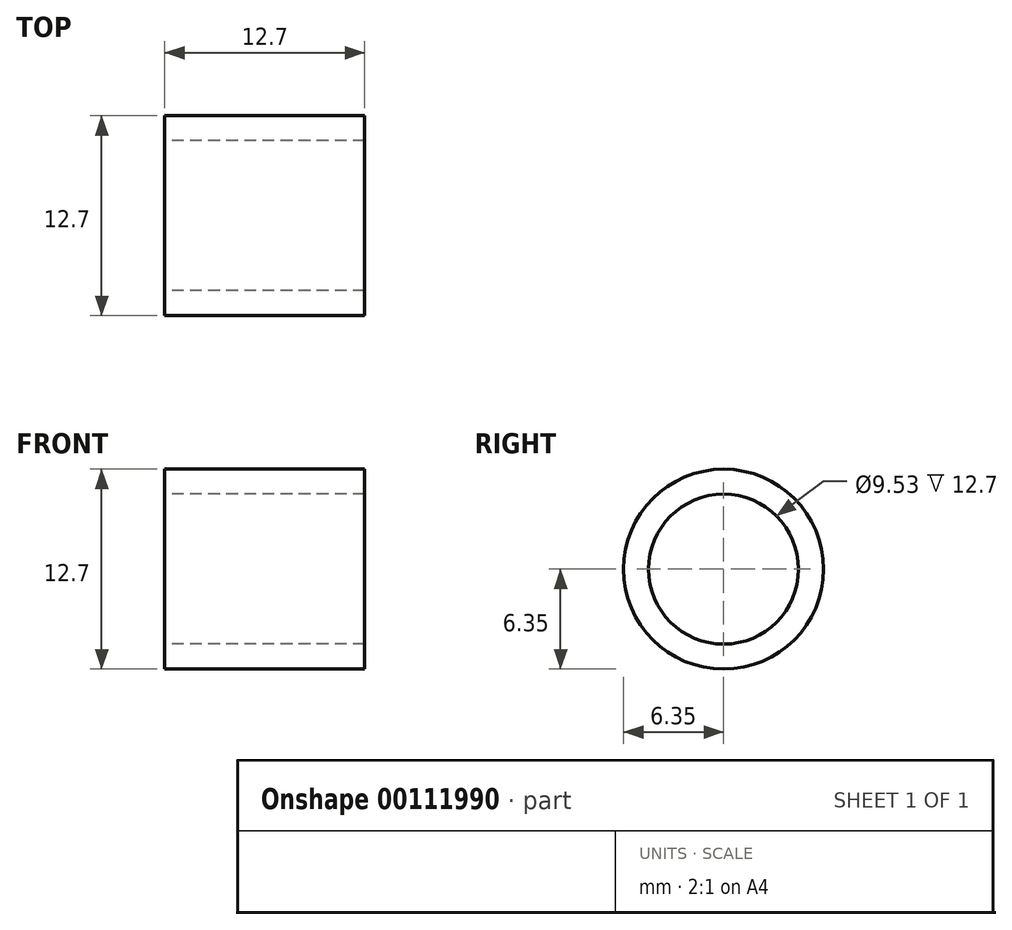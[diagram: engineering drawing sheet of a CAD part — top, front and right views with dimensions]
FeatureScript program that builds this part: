
annotation { "Feature Type Name" : "Feature", "Feature Type Description" : "" }
export const myFeature = defineFeature(function(context is Context, id is Id, definition is map)
    precondition{}
    {
        {
            var Q0;
            Q0=qCreatedBy(makeId("Right.planeOp"),FACE);
            var sketch = newSketch(context, id + "F0", { "sketchPlane" : qUnion([Q0])});
            skCircle(sketch, "E0", {"center": v(0, 0) * mm, "radius": 4.76 * mm});
            skCircle(sketch, "E1", {"center": v(0, 0) * mm, "radius": 6.35 * mm});
            skSolve(sketch);
        }
        {
            var Q0;
            Q0 = qSketchRegion(id + "F0", true);
            extrude(context, id + "F1", {"entities" : qUnion([Q0]), "depth" : 12.7 * mm});
        }
    });
